# Revit family: Shower-Shower_Trim-KOHLER-Pitch-K-TS97077-1
name_source: partatom
category: Plumbing Fixtures
revit_build: Autodesk Revit 2017 (Build: 20160225_1515(x64)
units: mm (PartAtom-declared; Revit-internal decimal feet)

## family parameters
Cut with Voids When Loaded = No
Host = Face
OmniClass Number = 23.31.17.00
OmniClass Title = Showers
Part Type = Normal
Room Calculation Point = No
Round Connector Dimension = Use Diameter
Shared = No

## types (5) — shared parameters
ADA Compliant = No
Assembly Code = D2010700
CW Connection = No
Cold Water Inlet = Cold Water Inlet
Date Modified = 02/26/2020
Default Elevation = 42"
Drain Included = No
Flow Rate = 2 GPM
HW Connection = Yes
Handle Clearance = 3 3/8"
Height = 6 3/8"
Length = 7 15/16"
Manufacturer = KOHLER Co.
MasterFormat 1995 = 15410
MasterFormat 2004 = 22.41.23
Material = Premium Metal Construction
Product Documentation Link = https://www.us.kohler.com
Product Name = Pitch
Product Page URL = http://www.us.kohler.com
Tempered  Water Inlet = Tempered  Water Inlet
URL = https://www.us.kohler.com
Vent Connection = No
Waste Connection = No
Waste Water Outlet = Waste Water Outlet
WaterSense Certified = Yes
Width = 6 3/8"

## per-type parameters (varying)
| type | Description | Finish | Model | Pressure | Type |
| 2 GPM, CP-Polished Chrome | Rite-Temp shower trim with 2.0 gpm showerhead | Kohler-Metal-CP-Polished_Chrome | K-TS97077-4-CP | 45.00 psi | 1 |
| 2 GPM, BN-Vibrant Brushed Nickel | Rite-Temp shower trim with 2.0 gpm showerhead | Kohler-Metal-BN-Vibrant_Brushed_Nickel | K-TS97077-4-BN | 45.00 psi | 2 |
| 2 GPM, BL-Matte Black | Rite-Temp shower trim with 2.0 gpm showerhead | Kohler-Metal-BL-Matte_Black | K-TS97077-4-BL | 45.00 psi | 3 |
| 1.75 GPM, CP-Polished Chrome | Rite-Temp shower trim with 1.75 gpm showerhead | Kohler-Metal-CP-Polished_Chrome | K-TS97077-4G-CP | 80.00 psi | 4 |
| 1.75 GPM, BN-Vibrant Brushed Nickel | Rite-Temp shower trim with 1.75 gpm showerhead | Kohler-Metal-BN-Vibrant_Brushed_Nickel | K-TS97077-4G-BN | 80.00 psi | 5 |

## geometry (parser evidence)
native form markers: Sweep x8
no freeform markers — native parametric forms only
